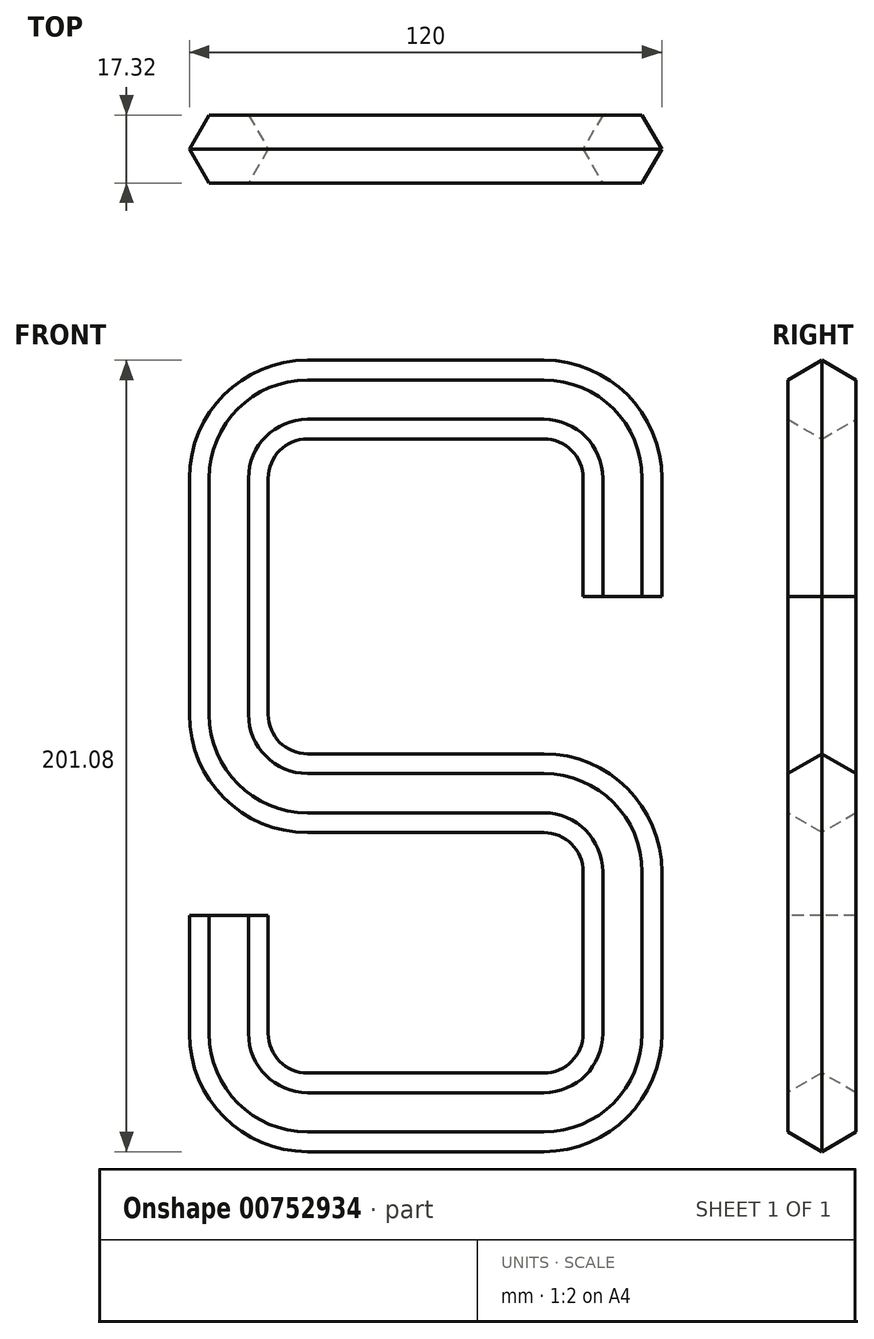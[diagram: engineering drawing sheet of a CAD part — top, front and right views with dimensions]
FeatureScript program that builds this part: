
annotation { "Feature Type Name" : "Feature", "Feature Type Description" : "" }
export const myFeature = defineFeature(function(context is Context, id is Id, definition is map)
    precondition{}
    {
        {
            var Q0;
            Q0=qCreatedBy(makeId("Front.planeOp"),FACE);
            var sketch = newSketch(context, id + "F0", { "sketchPlane" : qUnion([Q0])});
            skLineSegment(sketch, "E0", {"start": v(0, 0) * mm, "end": v(0, 30) * mm});
            skLineSegment(sketch, "E1", {"start": v(-20, 50) * mm, "end": v(-80, 50) * mm});
            skLineSegment(sketch, "E2", {"start": v(-100, 30) * mm, "end": v(-100, -30) * mm});
            skLineSegment(sketch, "E3", {"start": v(-80, -50) * mm, "end": v(-20, -50) * mm});
            skLineSegment(sketch, "E4", {"start": v(0, -70) * mm, "end": v(0, -111.08) * mm});
            skLineSegment(sketch, "E5", {"start": v(-20, -131.08) * mm, "end": v(-80, -131.08) * mm});
            skLineSegment(sketch, "E6", {"start": v(-100, -111.08) * mm, "end": v(-100, -81.08) * mm});
            skPoint(sketch, "E7.visualSharp", {"position": v(0, 50) * mm});
            skArc(sketch, "E7.filletArc", {"start": v(0, 30) * mm, "mid": v(-5.86, 44.14) * mm, "end": v(-20, 50) * mm});
            skPoint(sketch, "E8.visualSharp", {"position": v(-100, 50) * mm});
            skArc(sketch, "E8.filletArc", {"start": v(-80, 50) * mm, "mid": v(-94.14, 44.14) * mm, "end": v(-100, 30) * mm});
            skPoint(sketch, "E9.visualSharp", {"position": v(-100, -50) * mm});
            skArc(sketch, "E9.filletArc", {"start": v(-100, -30) * mm, "mid": v(-94.14, -44.14) * mm, "end": v(-80, -50) * mm});
            skPoint(sketch, "E10.visualSharp", {"position": v(0, -50) * mm});
            skArc(sketch, "E10.filletArc", {"start": v(0, -70) * mm, "mid": v(-5.86, -55.86) * mm, "end": v(-20, -50) * mm});
            skPoint(sketch, "E11.visualSharp", {"position": v(0, -131.08) * mm});
            skArc(sketch, "E11.filletArc", {"start": v(-20, -131.08) * mm, "mid": v(-5.86, -125.22) * mm, "end": v(0, -111.08) * mm});
            skPoint(sketch, "E12.visualSharp", {"position": v(-100, -131.08) * mm});
            skArc(sketch, "E12.filletArc", {"start": v(-100, -111.08) * mm, "mid": v(-94.14, -125.22) * mm, "end": v(-80, -131.08) * mm});
            skSolve(sketch);
        }
        {
            var Q0;
            Q0=qCreatedBy(makeId("Top.planeOp"),FACE);
            var sketch = newSketch(context, id + "F1", { "sketchPlane" : qUnion([Q0])});
            skLineSegment(sketch, "E13.0", {"start": v(-5, 8.66) * mm, "end": v(5, 8.66) * mm});
            skLineSegment(sketch, "E13.1", {"start": v(5, 8.66) * mm, "end": v(10, 0) * mm});
            skLineSegment(sketch, "E13.2", {"start": v(10, 0) * mm, "end": v(5, -8.66) * mm});
            skLineSegment(sketch, "E13.3", {"start": v(5, -8.66) * mm, "end": v(-5, -8.66) * mm});
            skLineSegment(sketch, "E13.4", {"start": v(-5, -8.66) * mm, "end": v(-10, 0) * mm});
            skLineSegment(sketch, "E13.5", {"start": v(-10, 0) * mm, "end": v(-5, 8.66) * mm});
            skPoint(sketch, "E13.0.midPoint", {"position": v(0, 8.66) * mm});
            skSolve(sketch);
        }
        {
            var Q0;
            Q0=makeQuery(id+"F1.imprint","IMPRINT",FACE,{"disambiguationData":[TD([[makeQuery(id+"F1.imprint","IMPRINT",EDGE,{"derivedFrom":sQuery(id+"F1.wireOp",EDGE,"E13.0")}),-1.0]])]});
            var Q1;
            Q1=sQuery(id+"F0.wireOp",EDGE,"E0");
            var Q2;
            Q2=sQuery(id+"F0.wireOp",EDGE,"E7.filletArc");
            var Q3;
            Q3=sQuery(id+"F0.wireOp",EDGE,"E1");
            var Q4;
            Q4=sQuery(id+"F0.wireOp",EDGE,"E8.filletArc");
            var Q5;
            Q5=sQuery(id+"F0.wireOp",EDGE,"E2");
            var Q6;
            Q6=sQuery(id+"F0.wireOp",EDGE,"E9.filletArc");
            var Q7;
            Q7=sQuery(id+"F0.wireOp",EDGE,"E3");
            var Q8;
            Q8=sQuery(id+"F0.wireOp",EDGE,"E10.filletArc");
            var Q9;
            Q9=sQuery(id+"F0.wireOp",EDGE,"E4");
            var Q10;
            Q10=sQuery(id+"F0.wireOp",EDGE,"E11.filletArc");
            var Q11;
            Q11=sQuery(id+"F0.wireOp",EDGE,"E5");
            var Q12;
            Q12=sQuery(id+"F0.wireOp",EDGE,"E12.filletArc");
            var Q13;
            Q13=sQuery(id+"F0.wireOp",EDGE,"E6");
            sweep(context, id + "F2", {"profiles" : qUnion([Q0]), "path" : qUnion([Q1, Q2, Q3, Q4, Q5, Q6, Q7, Q8, Q9, Q10, Q11, Q12, Q13])});
        }
    });
